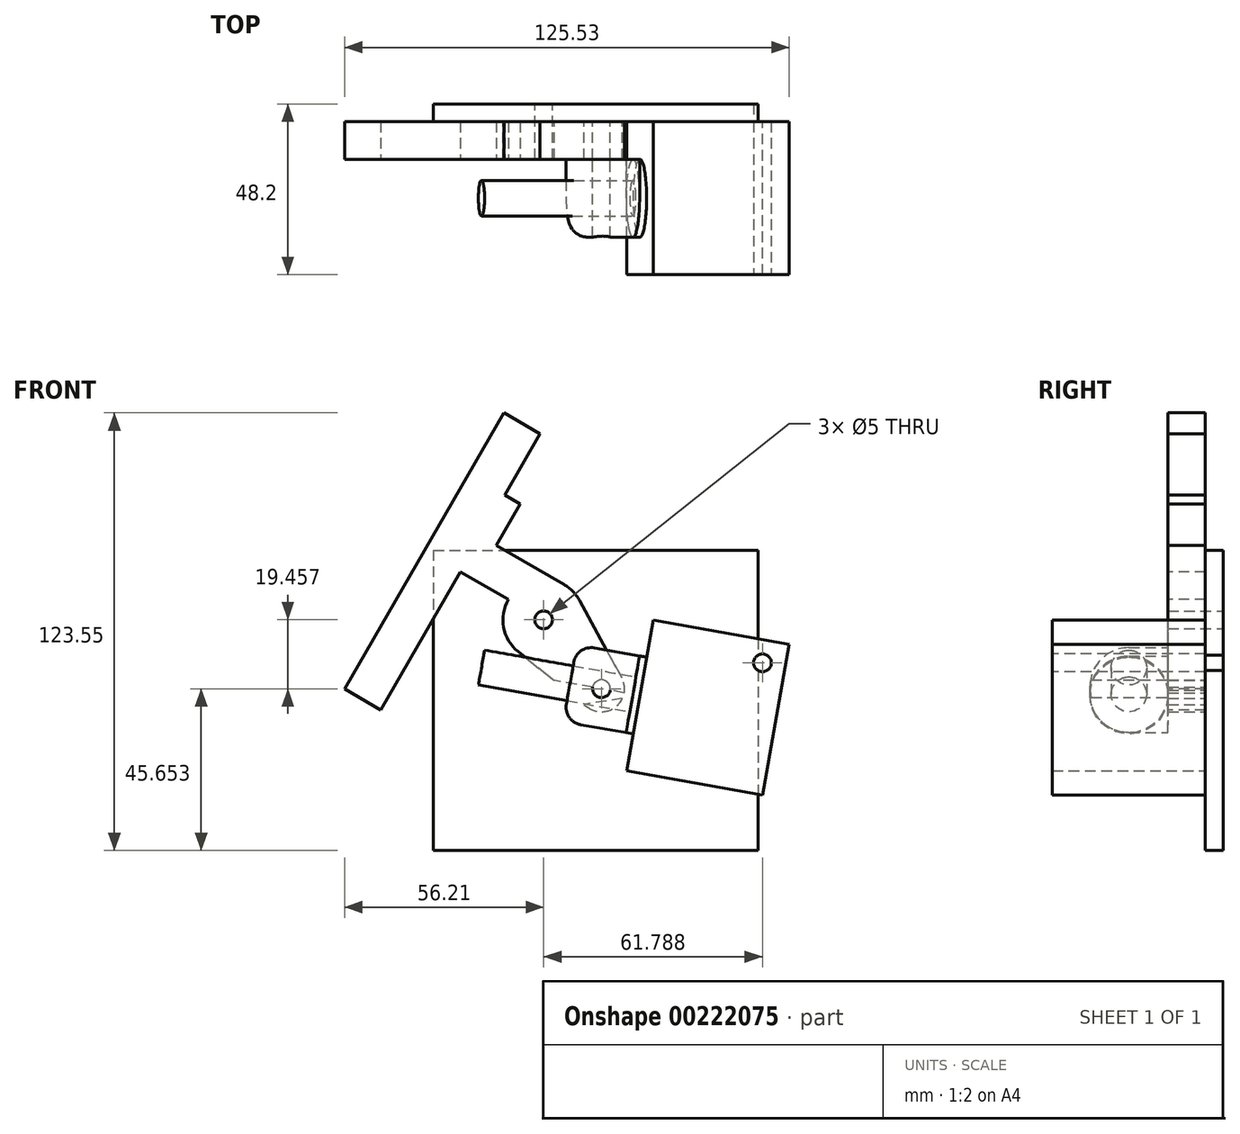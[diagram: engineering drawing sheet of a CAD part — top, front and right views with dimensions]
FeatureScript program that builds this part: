
annotation { "Feature Type Name" : "Feature", "Feature Type Description" : "" }
export const myFeature = defineFeature(function(context is Context, id is Id, definition is map)
    precondition{}
    {
        {
            var Q0;
            Q0=qCreatedBy(makeId("Front.planeOp"),FACE);
            var sketch = newSketch(context, id + "F0", { "sketchPlane" : qUnion([Q0])});
            skArc(sketch, "E0", {"start": v(10.1, 5.51) * mm, "mid": v(-7.4, 8.8) * mm, "end": v(-7.18, -8.98) * mm});
            skCircle(sketch, "E1", {"center": v(0, 0) * mm, "radius": 2.5 * mm});
            skLineSegment(sketch, "E2", {"start": v(-23.42, 12.9) * mm, "end": v(20.76, 12.9) * mm, "construction": true});
            skCircle(sketch, "E3", {"center": v(0, 0) * mm, "radius": 25.4 * mm, "construction": true});
            skLineSegment(sketch, "E4", {"start": v(0, 0) * mm, "end": v(16.33, -19.46) * mm, "construction": true});
            skLineSegment(sketch, "E5", {"start": v(16.33, -19.46) * mm, "end": v(27.16, -21.37) * mm, "construction": true});
            skLineSegment(sketch, "E6", {"start": v(27.16, -21.37) * mm, "end": v(29.07, -10.53) * mm, "construction": true});
            skLineSegment(sketch, "E7", {"start": v(25.25, -32.2) * mm, "end": v(27.16, -21.37) * mm, "construction": true});
            skLineSegment(sketch, "E8", {"start": v(27.16, -21.37) * mm, "end": v(30.91, -0.1) * mm});
            skLineSegment(sketch, "E9", {"start": v(27.16, -21.37) * mm, "end": v(23.4, -42.64) * mm});
            skLineSegment(sketch, "E10", {"start": v(23.4, -42.64) * mm, "end": v(61.82, -49.41) * mm});
            skLineSegment(sketch, "E11", {"start": v(30.91, -0.1) * mm, "end": v(69.32, -6.87) * mm});
            skLineSegment(sketch, "E12", {"start": v(69.32, -6.87) * mm, "end": v(61.82, -49.41) * mm});
            skArc(sketch, "E13", {"start": v(12.27, -24.53) * mm, "mid": v(20.5, -24.44) * mm, "end": v(22.03, -16.34) * mm});
            skLineSegment(sketch, "E14", {"start": v(-7.18, -8.98) * mm, "end": v(12.27, -24.53) * mm});
            skLineSegment(sketch, "E15", {"start": v(10.1, 5.51) * mm, "end": v(22.03, -16.34) * mm});
            skCircle(sketch, "E16", {"center": v(16.33, -19.46) * mm, "radius": 2.5 * mm});
            skCircle(sketch, "E17", {"center": v(-22, -12.7) * mm, "radius": 6.5 * mm});
            skPoint(sketch, "E18.startSnap0", {"position": v(-8.16, -9.73) * mm});
            skLineSegment(sketch, "E19", {"start": v(-13.13, -14.26) * mm, "end": v(-15.04, -25.1) * mm});
            skLineSegment(sketch, "E20", {"start": v(-15.04, -25.1) * mm, "end": v(-11.22, -3.43) * mm});
            skLineSegment(sketch, "E21", {"start": v(-11.22, -3.43) * mm, "end": v(-24.03, -1.17) * mm});
            skLineSegment(sketch, "E22", {"start": v(-29.82, -5.23) * mm, "end": v(-31.9, -17.05) * mm});
            skLineSegment(sketch, "E23", {"start": v(-27.85, -22.84) * mm, "end": v(-15.04, -25.1) * mm});
            skPoint(sketch, "E24.visualSharp", {"position": v(-28.95, -0.3) * mm});
            skArc(sketch, "E24.filletArc", {"start": v(-24.03, -1.17) * mm, "mid": v(-27.76, -2) * mm, "end": v(-29.82, -5.23) * mm});
            skPoint(sketch, "E25.visualSharp", {"position": v(-32.77, -21.97) * mm});
            skArc(sketch, "E25.filletArc", {"start": v(-31.9, -17.05) * mm, "mid": v(-31.07, -20.78) * mm, "end": v(-27.85, -22.84) * mm});
            skLineSegment(sketch, "E26", {"start": v(-27.76, 12.9) * mm, "end": v(-49.26, -46.16) * mm, "construction": true});
            skLineSegment(sketch, "E27", {"start": v(27.16, -21.37) * mm, "end": v(-22, -12.7) * mm});
            skLineSegment(sketch, "E28", {"start": v(-22, -12.7) * mm, "end": v(0, 0) * mm, "construction": true});
            skLineSegment(sketch, "E29", {"start": v(18.09, 12.9) * mm, "end": v(75.65, -20.33) * mm, "construction": true});
            skLineSegment(sketch, "E30", {"start": v(49.22, -48.64) * mm, "end": v(-24.78, -48.64) * mm});
            skLineSegment(sketch, "E31", {"start": v(-24.78, -48.64) * mm, "end": v(-24.78, -64.64) * mm});
            skLineSegment(sketch, "E32", {"start": v(-24.78, -64.64) * mm, "end": v(49.22, -64.64) * mm});
            skLineSegment(sketch, "E33", {"start": v(49.22, -64.64) * mm, "end": v(49.22, -48.64) * mm});
            skLineSegment(sketch, "E34", {"start": v(0, 0) * mm, "end": v(15, 25.98) * mm});
            skLineSegment(sketch, "E35", {"start": v(15, 25.98) * mm, "end": v(-23.97, 48.48) * mm});
            skLineSegment(sketch, "E36", {"start": v(15, 25.98) * mm, "end": v(19.33, 23.48) * mm});
            skLineSegment(sketch, "E37", {"start": v(19.33, 23.48) * mm, "end": v(25.33, 33.87) * mm});
            skLineSegment(sketch, "E38", {"start": v(25.33, 33.87) * mm, "end": v(-17.97, 58.87) * mm});
            skLineSegment(sketch, "E39", {"start": v(-23.97, 48.48) * mm, "end": v(-17.97, 58.87) * mm});
            skLineSegment(sketch, "E40", {"start": v(27.16, -21.37) * mm, "end": v(0, -25.72) * mm});
            skSolve(sketch);
        }
        {
            var Q0;
            Q0=makeQuery(id+"F0.imprint","IMPRINT",FACE,{"disambiguationData":[TD([[makeQuery(id+"F0.imprint","IMPRINT",EDGE,{"derivedFrom":sQuery(id+"F0.wireOp",EDGE,"E0")}),1.0]])]});
            var Q1;
            {var subQ0=sQuery(id+"F0.wireOp",EDGE,"E21");var subQ1=sQuery(id+"F0.wireOp",EDGE,"E14");var subQ2=makeQuery(id+"F0.imprint","INTERSECT",VERTEX,{"derivedFrom":[subQ1,subQ0]});Q1=makeQuery(id+"F0.imprint","IMPRINT",FACE,{"disambiguationData":[TD([[makeQuery(id+"F0.imprint","IMPRINT",EDGE,{"disambiguationData":[TD([[subQ2,-1.0]])],"derivedFrom":subQ1}),1.0]])]});}
            var Q2;
            {var subQ1=sQuery(id+"F0.wireOp",EDGE,"E13");var subQ6=sQuery(id+"F0.wireOp",EDGE,"E14");var subQ7=makeQuery(id+"F0.imprint","INTERSECT",VERTEX,{"derivedFrom":[subQ1,subQ6]});Q2=makeQuery(id+"F0.imprint","IMPRINT",FACE,{"disambiguationData":[TD([[makeQuery(id+"F0.imprint","IMPRINT",EDGE,{"disambiguationData":[TD([[subQ7,-1.0]])],"derivedFrom":subQ1}),1.0]])]});}
            extrude(context, id + "F1", {"entities" : qUnion([Q0, Q1, Q2]), "depth" : 10.6 * mm, "offsetDistance" : 25 * mm});
        }
        {
            var Q0;
            Q0=makeQuery(id+"F0.imprint","IMPRINT",FACE,{"disambiguationData":[TD([[makeQuery(id+"F0.imprint","IMPRINT",EDGE,{"derivedFrom":sQuery(id+"F0.wireOp",EDGE,"E8")}),-1.0]])]});
            extrude(context, id + "F2", {"entities" : qUnion([Q0]), "depth" : 43.2 * mm, "offsetDistance" : 25 * mm});
        }
        {
            var Q0;
            Q0=makeQuery(id+"F2.opExtrude","SWEPT_FACE",FACE,{"disambiguationData":[OSD([sQuery(id+"F0.wireOp",EDGE,"E8"),sQuery(id+"F0.wireOp",EDGE,"E9")])]});
            var sketch = newSketch(context, id + "F3", { "sketchPlane" : qUnion([Q0])});
            skCircle(sketch, "E41", {"center": v(21.6, -16.33) * mm, "radius": 11 * mm});
            skPoint(sketch, "E41.centerSnap0", {"position": v(43.2, -16.33) * mm});
            skPoint(sketch, "E41.centerSnap1", {"position": v(21.6, 5.27) * mm});
            skSolve(sketch);
        }
        {
            var Q0;
            Q0=makeQuery(id+"F3.imprint","IMPRINT",FACE,{"disambiguationData":[TD([[makeQuery(id+"F3.imprint","IMPRINT",EDGE,{"derivedFrom":sQuery(id+"F3.wireOp",EDGE,"E41")}),1.0]])]});
            extrude(context, id + "F4", {"entities" : qUnion([Q0]), "operationType" : NewBodyOperationType.ADD, "depth" : 2 * mm, "offsetDistance" : 25 * mm});
        }
        {
            var Q0;
            Q0=makeQuery(id+"F4.opExtrude","CAP_FACE",FACE,{"disambiguationData":[OSD([sQuery(id+"F3.wireOp",EDGE,"E41")])],"isStart":false});
            var sketch = newSketch(context, id + "F5", { "sketchPlane" : qUnion([Q0])});
            skCircle(sketch, "E42.0", {"center": v(21.6, -16.33) * mm, "radius": 11 * mm});
            skCircle(sketch, "E43", {"center": v(21.6, -16.33) * mm, "radius": 5 * mm});
            skSolve(sketch);
        }
        {
            var Q0;
            Q0=makeQuery(id+"F5.imprint","IMPRINT",FACE,{"disambiguationData":[TD([[makeQuery(id+"F5.imprint","IMPRINT",EDGE,{"derivedFrom":sQuery(id+"F5.wireOp",EDGE,"E43")}),1.0]])]});
            extrude(context, id + "F6", {"entities" : qUnion([Q0]), "operationType" : NewBodyOperationType.ADD, "depth" : (45.4 - 2) * mm, "offsetDistance" : 25 * mm});
        }
        {
            var Q0;
            Q0=makeQuery(id+"F1.opExtrude","CAP_FACE",FACE,{"disambiguationData":[OSD([sQuery(id+"F0.wireOp",EDGE,"E0"),sQuery(id+"F0.wireOp",EDGE,"E1"),sQuery(id+"F0.wireOp",EDGE,"E13"),sQuery(id+"F0.wireOp",EDGE,"E14"),sQuery(id+"F0.wireOp",EDGE,"E15"),sQuery(id+"F0.wireOp",EDGE,"E16")])],"isStart":false});
            var sketch = newSketch(context, id + "F7", { "sketchPlane" : qUnion([Q0])});
            skCircle(sketch, "E44.0", {"center": v(16.33, -19.46) * mm, "radius": 2.5 * mm});
            skLineSegment(sketch, "E45.0", {"start": v(23.28, -31.85) * mm, "end": v(27.1, -10.19) * mm});
            skLineSegment(sketch, "E46", {"start": v(27.1, -10.19) * mm, "end": v(9.37, -7.06) * mm});
            skLineSegment(sketch, "E47", {"start": v(23.28, -31.85) * mm, "end": v(5.55, -28.73) * mm});
            skLineSegment(sketch, "E48", {"start": v(9.37, -7.06) * mm, "end": v(5.55, -28.73) * mm});
            skSolve(sketch);
        }
        {
            var Q0;
            {var subQ1=sQuery(id+"F7.wireOp",EDGE,"E47");Q0=makeQuery(id+"F7.imprint","IMPRINT",FACE,{"disambiguationData":[TD([[makeQuery(id+"F7.imprint","IMPRINT",EDGE,{"derivedFrom":subQ1}),-1.0]])]});}
            var Q1;
            Q1=makeQuery(id+"F7.imprint","IMPRINT",FACE,{"disambiguationData":[TD([[makeQuery(id+"F7.imprint","IMPRINT",EDGE,{"derivedFrom":sQuery(id+"F7.wireOp",EDGE,"E44.0")}),-1.0]])]});
            var Q2;
            {var subQ0=sQuery(id+"F7.wireOp",EDGE,"E46");var subQ1=sQuery(id+"F7.wireOp",EDGE,"E45.0");var subQ2=makeQuery(id+"F7.imprint","INTERSECT",VERTEX,{"derivedFrom":[subQ1,subQ0]});Q2=makeQuery(id+"F7.imprint","IMPRINT",FACE,{"disambiguationData":[TD([[makeQuery(id+"F7.imprint","IMPRINT",EDGE,{"disambiguationData":[TD([[subQ2,1.0]])],"derivedFrom":subQ1}),1.0]])]});}
            var Q3;
            {var subQ8=sQuery(id+"F0.wireOp",EDGE,"E13");var subQ9=makeQuery(id+"F1.opExtrude","CAP_EDGE",EDGE,{"disambiguationData":[OSD([subQ8])],"isStart":false});Q3=makeQuery(id+"F7.imprint","IMPRINT",FACE,{"disambiguationData":[TD([[makeQuery(id+"F7.imprint","IMPRINT",EDGE,{"derivedFrom":subQ9}),1.0]])]});}
            extrude(context, id + "F8", {"entities" : qUnion([Q0, Q1, Q2, Q3]), "depth" : 22 * mm, "offsetDistance" : 25 * mm});
        }
        {
            var Q0;
            Q0=makeQuery(id+"F8.opExtrude","CAP_EDGE",EDGE,{"disambiguationData":[OSD([sQuery(id+"F7.wireOp",EDGE,"E46")])],"isStart":false});
            var Q1;
            Q1=makeQuery(id+"F8.opExtrude","CAP_EDGE",EDGE,{"disambiguationData":[OSD([sQuery(id+"F7.wireOp",EDGE,"E47")])],"isStart":false});
            fillet(context, id + "F9", {"entities" : qUnion([Q0, Q1]), "radius" : 11 * mm, "tangentPropagation" : true, "allowEdgeOverflow" : false});
        }
        {
            var Q0;
            Q0=makeQuery(id+"F0.imprint","IMPRINT",FACE,{"disambiguationData":[TD([[makeQuery(id+"F0.imprint","IMPRINT",EDGE,{"derivedFrom":sQuery(id+"F0.wireOp",EDGE,"E0")}),1.0]])]});
            var sketch = newSketch(context, id + "F10", { "sketchPlane" : qUnion([Q0])});
            skLineSegment(sketch, "E49.bottom", {"start": v(-31.15, 19.66) * mm, "end": v(60.52, 19.66) * mm});
            skLineSegment(sketch, "E49.top", {"start": v(-31.15, -65.11) * mm, "end": v(60.52, -65.11) * mm});
            skLineSegment(sketch, "E49.left", {"start": v(-31.15, 19.66) * mm, "end": v(-31.15, -65.11) * mm});
            skLineSegment(sketch, "E49.right", {"start": v(60.52, 19.66) * mm, "end": v(60.52, -65.11) * mm});
            skSolve(sketch);
        }
        {
            var Q0;
            Q0=makeQuery(id+"F10.imprint","IMPRINT",FACE,{"disambiguationData":[TD([[makeQuery(id+"F10.imprint","IMPRINT",EDGE,{"derivedFrom":sQuery(id+"F10.wireOp",EDGE,"E49.bottom")}),-1.0]])]});
            var Q1;
            Q1=makeQuery(id+"F0.imprint","IMPRINT",FACE,{"disambiguationData":[TD([[makeQuery(id+"F0.imprint","IMPRINT",EDGE,{"derivedFrom":sQuery(id+"F0.wireOp",EDGE,"E0")}),1.0]])]});
            var Q2;
            Q2=makeQuery(id+"F0.imprint","IMPRINT",FACE,{"disambiguationData":[TD([[makeQuery(id+"F0.imprint","IMPRINT",EDGE,{"derivedFrom":sQuery(id+"F0.wireOp",EDGE,"E16")}),1.0]])]});
            extrude(context, id + "F11", {"entities" : qUnion([Q0, Q1, Q2]), "oppositeDirection" : true, "depth" : 5 * mm, "offsetDistance" : 25 * mm});
        }
        {
            var Q0;
            Q0=makeQuery(id+"F2.opExtrude","CAP_FACE",FACE,{"disambiguationData":[OSD([sQuery(id+"F0.wireOp",EDGE,"E8"),sQuery(id+"F0.wireOp",EDGE,"E9"),sQuery(id+"F0.wireOp",EDGE,"E10"),sQuery(id+"F0.wireOp",EDGE,"E11"),sQuery(id+"F0.wireOp",EDGE,"E12")])],"isStart":false});
            var sketch = newSketch(context, id + "F12", { "sketchPlane" : qUnion([Q0])});
            skCircle(sketch, "E50", {"center": v(61.79, -12.14) * mm, "radius": 6.5 * mm});
            skCircle(sketch, "E51", {"center": v(61.79, -12.14) * mm, "radius": 2.5 * mm});
            skSolve(sketch);
        }
        {
            var Q0;
            Q0=makeQuery(id+"F12.imprint","IMPRINT",FACE,{"disambiguationData":[TD([[makeQuery(id+"F12.imprint","IMPRINT",EDGE,{"derivedFrom":sQuery(id+"F12.wireOp",EDGE,"E51")}),1.0]])]});
            extrude(context, id + "F13", {"entities" : qUnion([Q0]), "operationType" : NewBodyOperationType.REMOVE, "oppositeDirection" : true, "depth" : 74.8 * mm, "offsetDistance" : 25 * mm});
        }
        {
            var Q0;
            Q0=makeQuery(id+"F1.opExtrude","CAP_FACE",FACE,{"disambiguationData":[OSD([sQuery(id+"F0.wireOp",EDGE,"E0"),sQuery(id+"F0.wireOp",EDGE,"E1"),sQuery(id+"F0.wireOp",EDGE,"E13"),sQuery(id+"F0.wireOp",EDGE,"E14"),sQuery(id+"F0.wireOp",EDGE,"E15"),sQuery(id+"F0.wireOp",EDGE,"E16")])],"isStart":false});
            var sketch = newSketch(context, id + "F14", { "sketchPlane" : qUnion([Q0])});
            skLineSegment(sketch, "E52", {"start": v(-24.91, 1.1) * mm, "end": v(-31.66, -10.59) * mm});
            skLineSegment(sketch, "E53", {"start": v(-31.66, -10.59) * mm, "end": v(-36, -8.09) * mm});
            skLineSegment(sketch, "E54", {"start": v(-36, -8.09) * mm, "end": v(-17.74, 23.52) * mm});
            skLineSegment(sketch, "E55", {"start": v(-13.41, 21.02) * mm, "end": v(5.75, 9.96) * mm});
            skArc(sketch, "E56.0", {"start": v(10.1, 5.51) * mm, "mid": v(-7.4, 8.8) * mm, "end": v(-7.18, -8.98) * mm});
            skLineSegment(sketch, "E57", {"start": v(-24.91, 1.1) * mm, "end": v(-7.83, -8.76) * mm});
            skLineSegment(sketch, "E58.0", {"start": v(-18.42, -18.4) * mm, "end": v(-16.68, -8.56) * mm});
            skLineSegment(sketch, "E59", {"start": v(-13.41, 21.02) * mm, "end": v(-6.66, 32.72) * mm});
            skLineSegment(sketch, "E60", {"start": v(-17.74, 23.52) * mm, "end": v(-11, 35.22) * mm});
            skLineSegment(sketch, "E61", {"start": v(-11, 35.22) * mm, "end": v(-6.66, 32.72) * mm});
            skLineSegment(sketch, "E62", {"start": v(-1, 52.54) * mm, "end": v(-46, -25.4) * mm});
            skLineSegment(sketch, "E63", {"start": v(-46, -25.4) * mm, "end": v(-56.21, -19.5) * mm});
            skLineSegment(sketch, "E64", {"start": v(-56.21, -19.5) * mm, "end": v(-11.21, 58.44) * mm});
            skLineSegment(sketch, "E65", {"start": v(-1, 52.54) * mm, "end": v(-11.21, 58.44) * mm});
            skLineSegment(sketch, "E66", {"start": v(0, 0) * mm, "end": v(-23.5, 13.56) * mm});
            skLineSegment(sketch, "E67", {"start": v(-36, -8.09) * mm, "end": v(-41.62, -4.84) * mm});
            skLineSegment(sketch, "E68", {"start": v(-41.62, -4.84) * mm, "end": v(-16.62, 38.47) * mm});
            skLineSegment(sketch, "E69", {"start": v(-11, 35.22) * mm, "end": v(-16.62, 38.47) * mm});
            skLineSegment(sketch, "E70.0", {"start": v(-9.26, -6.82) * mm, "end": v(-9.26, -6.82) * mm});
            skLineSegment(sketch, "E71.bottom", {"start": v(46.42, -51.41) * mm, "end": v(3.22, -51.41) * mm, "construction": true});
            skLineSegment(sketch, "E71.top", {"start": v(46.42, 1.59) * mm, "end": v(3.22, 1.59) * mm, "construction": true});
            skLineSegment(sketch, "E71.left", {"start": v(46.42, -51.41) * mm, "end": v(46.42, 1.59) * mm, "construction": true});
            skLineSegment(sketch, "E71.right", {"start": v(3.22, -51.41) * mm, "end": v(3.22, 1.59) * mm, "construction": true});
            skPoint(sketch, "E71.middle", {"position": v(24.82, -24.91) * mm});
            skLineSegment(sketch, "E72.bottom", {"start": v(63.82, -51.41) * mm, "end": v(-14.18, -51.41) * mm, "construction": true});
            skLineSegment(sketch, "E72.top", {"start": v(63.82, -69.41) * mm, "end": v(-14.18, -69.41) * mm, "construction": true});
            skLineSegment(sketch, "E72.left", {"start": v(63.82, -51.41) * mm, "end": v(63.82, -69.41) * mm, "construction": true});
            skLineSegment(sketch, "E72.right", {"start": v(-14.18, -51.41) * mm, "end": v(-14.18, -69.41) * mm, "construction": true});
            skPoint(sketch, "E72.middle", {"position": v(24.82, -60.41) * mm});
            skPoint(sketch, "E72.middle.positionSnap0", {"position": v(24.82, -51.41) * mm});
            skPoint(sketch, "E72.cornerSnap0", {"position": v(24.82, -51.41) * mm});
            skPoint(sketch, "E72.centerSnap0", {"position": v(24.82, -51.41) * mm});
            skCircle(sketch, "E73", {"center": v(0, 0) * mm, "radius": 24.94 * mm, "construction": true});
            skLineSegment(sketch, "E74", {"start": v(-23.42, -14.9) * mm, "end": v(-23.42, -49.9) * mm});
            skLineSegment(sketch, "E75", {"start": v(-24.94, 0) * mm, "end": v(-23.42, -14.9) * mm});
            skLineSegment(sketch, "E76.0", {"start": v(30.91, -0.1) * mm, "end": v(69.32, -6.87) * mm});
            skLineSegment(sketch, "E77", {"start": v(24.94, 0) * mm, "end": v(73.32, -8.53) * mm});
            skLineSegment(sketch, "E78", {"start": v(73.32, -8.53) * mm, "end": v(73.32, -49.9) * mm});
            skPoint(sketch, "E79.start.orphan", {"position": v(63.82, -46.38) * mm});
            skLineSegment(sketch, "E80.0", {"start": v(23.4, -42.64) * mm, "end": v(61.82, -49.41) * mm});
            skSolve(sketch);
        }
        {
            var Q0;
            Q0=makeQuery(id+"F14.imprint","IMPRINT",FACE,{"disambiguationData":[TD([[makeQuery(id+"F14.imprint","IMPRINT",EDGE,{"derivedFrom":sQuery(id+"F14.wireOp",EDGE,"E52")}),-1.0]])]});
            var Q1;
            {var subQ2=sQuery(id+"F14.wireOp",EDGE,"E55");Q1=makeQuery(id+"F14.imprint","IMPRINT",FACE,{"disambiguationData":[TD([[makeQuery(id+"F14.imprint","IMPRINT",EDGE,{"derivedFrom":subQ2}),-1.0]])]});}
            var Q2;
            {var subQ0=sQuery(id+"F14.wireOp",EDGE,"E67");Q2=makeQuery(id+"F14.imprint","IMPRINT",FACE,{"disambiguationData":[TD([[makeQuery(id+"F14.imprint","IMPRINT",EDGE,{"derivedFrom":subQ0}),-1.0]])]});}
            var Q3;
            {var subQ0=sQuery(id+"F14.wireOp",EDGE,"E63");Q3=makeQuery(id+"F14.imprint","IMPRINT",FACE,{"disambiguationData":[TD([[makeQuery(id+"F14.imprint","IMPRINT",EDGE,{"derivedFrom":subQ0}),-1.0]])]});}
            extrude(context, id + "F15", {"entities" : qUnion([Q0, Q1, Q2, Q3]), "operationType" : NewBodyOperationType.ADD, "oppositeDirection" : true, "depth" : 10.6 * mm, "offsetDistance" : 25 * mm});
        }
        {
            var Q0;
            Q0=makeQuery(id+"F9.opFillet","BLEND_EDGE",EDGE,{"blendedFrom":[makeQuery(id+"F8.opExtrude","CAP_EDGE",EDGE,{"disambiguationData":[OSD([sQuery(id+"F7.wireOp",EDGE,"E46")])],"isStart":false}),makeQuery(id+"F8.opExtrude","SWEPT_FACE",FACE,{"disambiguationData":[OSD([sQuery(id+"F7.wireOp",EDGE,"E48")])]})],"blendedInto":[makeQuery(id+"F8.opExtrude","SWEPT_FACE",FACE,{"disambiguationData":[OSD([sQuery(id+"F7.wireOp",EDGE,"E48")])]})]});
            fillet(context, id + "F16", {"entities" : qUnion([Q0]), "radius" : 5 * mm, "tangentPropagation" : true, "allowEdgeOverflow" : false});
        }
    });
